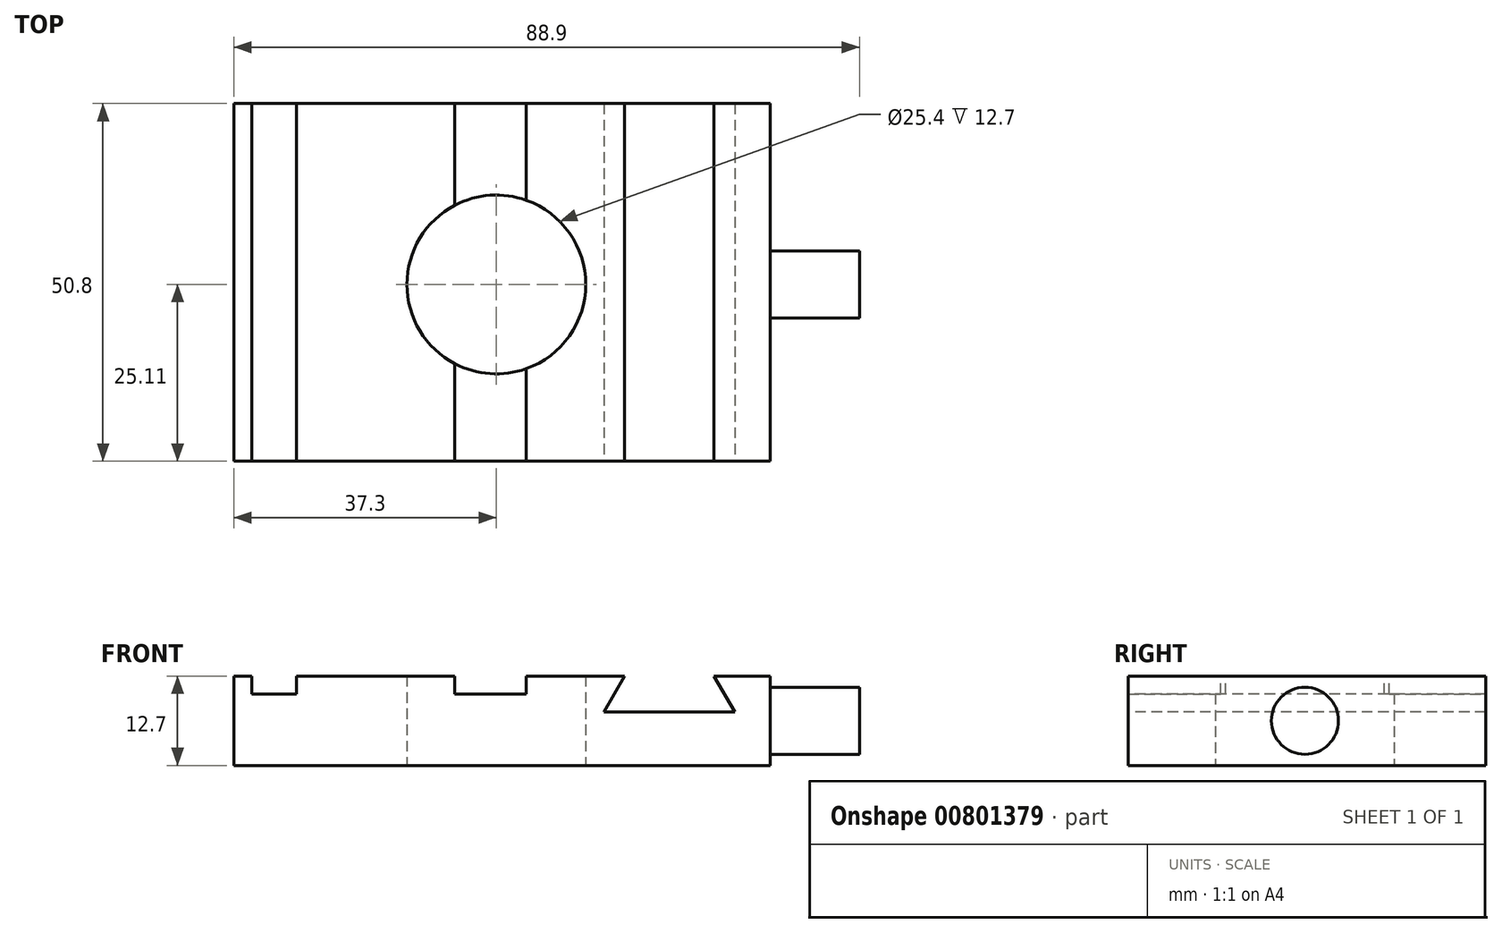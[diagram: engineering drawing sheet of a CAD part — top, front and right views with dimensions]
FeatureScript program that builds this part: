
annotation { "Feature Type Name" : "Feature", "Feature Type Description" : "" }
export const myFeature = defineFeature(function(context is Context, id is Id, definition is map)
    precondition{}
    {
        {
            var Q0;
            Q0=qCreatedBy(makeId("Top.planeOp"),FACE);
            var sketch = newSketch(context, id + "F0", { "sketchPlane" : qUnion([Q0])});
            skLineSegment(sketch, "E0.bottom", {"start": v(-37.3, 25.69) * mm, "end": v(38.9, 25.69) * mm});
            skLineSegment(sketch, "E0.top", {"start": v(-37.3, -25.11) * mm, "end": v(38.9, -25.11) * mm});
            skLineSegment(sketch, "E0.left", {"start": v(-37.3, 25.69) * mm, "end": v(-37.3, -25.11) * mm});
            skLineSegment(sketch, "E0.right", {"start": v(38.9, 25.69) * mm, "end": v(38.9, -25.11) * mm});
            skCircle(sketch, "E1", {"center": v(0, 0) * mm, "radius": 12.7 * mm});
            skSolve(sketch);
        }
        {
            var Q0;
            Q0=makeQuery(id+"F0.imprint","IMPRINT",FACE,{"disambiguationData":[TD([[makeQuery(id+"F0.imprint","IMPRINT",EDGE,{"derivedFrom":sQuery(id+"F0.wireOp",EDGE,"E0.bottom")}),-1.0]])]});
            extrude(context, id + "F1", {"entities" : qUnion([Q0]), "depth" : 12.7 * mm, "offsetDistance" : 25.4 * mm});
        }
        {
            var Q0;
            Q0=makeQuery(id+"F1.opExtrude","CAP_FACE",FACE,{"disambiguationData":[OSD([sQuery(id+"F0.wireOp",EDGE,"E0.bottom"),sQuery(id+"F0.wireOp",EDGE,"E0.top"),sQuery(id+"F0.wireOp",EDGE,"E0.left"),sQuery(id+"F0.wireOp",EDGE,"E0.right"),sQuery(id+"F0.wireOp",EDGE,"E1")])],"isStart":false});
            var sketch = newSketch(context, id + "F2", { "sketchPlane" : qUnion([Q0])});
            skLineSegment(sketch, "E2.bottom", {"start": v(-34.76, 25.69) * mm, "end": v(-28.41, 25.69) * mm});
            skLineSegment(sketch, "E2.top", {"start": v(-34.76, -25.11) * mm, "end": v(-28.41, -25.11) * mm});
            skLineSegment(sketch, "E2.left", {"start": v(-34.76, 25.69) * mm, "end": v(-34.76, -25.11) * mm});
            skLineSegment(sketch, "E2.right", {"start": v(-28.41, 25.69) * mm, "end": v(-28.41, -25.11) * mm});
            skLineSegment(sketch, "E3", {"start": v(-5.9, 25.69) * mm, "end": v(-5.9, -25.11) * mm});
            skLineSegment(sketch, "E4", {"start": v(-5.9, -25.11) * mm, "end": v(4.27, -25.11) * mm});
            skLineSegment(sketch, "E5", {"start": v(4.27, -25.11) * mm, "end": v(4.27, 25.69) * mm});
            skLineSegment(sketch, "E6", {"start": v(4.27, 25.69) * mm, "end": v(-5.9, 25.69) * mm});
            skPoint(sketch, "E7", {"position": v(0, 0) * mm});
            skLineSegment(sketch, "E8", {"start": v(-0.81, 25.69) * mm, "end": v(0.8, -25.11) * mm, "construction": true});
            skSolve(sketch);
        }
        {
            var Q0;
            Q0=makeQuery(id+"F2.imprint","IMPRINT",FACE,{"disambiguationData":[TD([[makeQuery(id+"F2.imprint","IMPRINT",EDGE,{"derivedFrom":sQuery(id+"F2.wireOp",EDGE,"E2.bottom")}),-1.0]])]});
            var Q1;
            {var subQ0=sQuery(id+"F2.wireOp",EDGE,"E4");Q1=makeQuery(id+"F2.imprint","IMPRINT",FACE,{"disambiguationData":[TD([[makeQuery(id+"F2.imprint","IMPRINT",EDGE,{"derivedFrom":subQ0}),1.0]])]});}
            var Q2;
            {var subQ0=sQuery(id+"F2.wireOp",EDGE,"E6");Q2=makeQuery(id+"F2.imprint","IMPRINT",FACE,{"disambiguationData":[TD([[makeQuery(id+"F2.imprint","IMPRINT",EDGE,{"derivedFrom":subQ0}),-1.0]])]});}
            extrude(context, id + "F3", {"entities" : qUnion([Q0, Q1, Q2]), "operationType" : NewBodyOperationType.REMOVE, "oppositeDirection" : true, "depth" : 2.54 * mm, "offsetDistance" : 25.4 * mm});
        }
        {
            var Q0;
            Q0=makeQuery(id+"F1.opExtrude","SWEPT_FACE",FACE,{"disambiguationData":[OSD([sQuery(id+"F0.wireOp",EDGE,"E0.top")])]});
            var sketch = newSketch(context, id + "F4", { "sketchPlane" : qUnion([Q0])});
            skLineSegment(sketch, "E9", {"start": v(18.24, 12.7) * mm, "end": v(15.3, 7.62) * mm});
            skLineSegment(sketch, "E10", {"start": v(15.3, 7.62) * mm, "end": v(33.87, 7.62) * mm});
            skLineSegment(sketch, "E11", {"start": v(33.87, 7.62) * mm, "end": v(30.94, 12.7) * mm});
            skLineSegment(sketch, "E12", {"start": v(30.94, 12.7) * mm, "end": v(18.24, 12.7) * mm});
            skLineSegment(sketch, "E13", {"start": v(24.59, 7.62) * mm, "end": v(24.59, 12.7) * mm, "construction": true});
            skSolve(sketch);
        }
        {
            var Q0;
            Q0=makeQuery(id+"F4.imprint","IMPRINT",FACE,{"disambiguationData":[TD([[makeQuery(id+"F4.imprint","IMPRINT",EDGE,{"derivedFrom":sQuery(id+"F4.wireOp",EDGE,"E9")}),1.0]])]});
            extrude(context, id + "F5", {"entities" : qUnion([Q0]), "operationType" : NewBodyOperationType.REMOVE, "endBound" : BoundingType.THROUGH_ALL, "oppositeDirection" : true, "depth" : 25.4 * mm, "offsetDistance" : 25.4 * mm});
        }
        {
            var Q0;
            Q0=makeQuery(id+"F1.opExtrude","SWEPT_FACE",FACE,{"disambiguationData":[OSD([sQuery(id+"F0.wireOp",EDGE,"E0.right")])]});
            var sketch = newSketch(context, id + "F6", { "sketchPlane" : qUnion([Q0])});
            skCircle(sketch, "E14", {"center": v(0, 6.35) * mm, "radius": 4.76 * mm});
            skPoint(sketch, "E14.centerSnap0", {"position": v(-25.11, 6.35) * mm});
            skSolve(sketch);
        }
        {
            var Q0;
            Q0=makeQuery(id+"F6.imprint","IMPRINT",FACE,{"disambiguationData":[TD([[makeQuery(id+"F6.imprint","IMPRINT",EDGE,{"derivedFrom":sQuery(id+"F6.wireOp",EDGE,"E14")}),1.0]])]});
            extrude(context, id + "F7", {"entities" : qUnion([Q0]), "operationType" : NewBodyOperationType.ADD, "depth" : 12.7 * mm, "offsetDistance" : 25.4 * mm});
        }
    });
